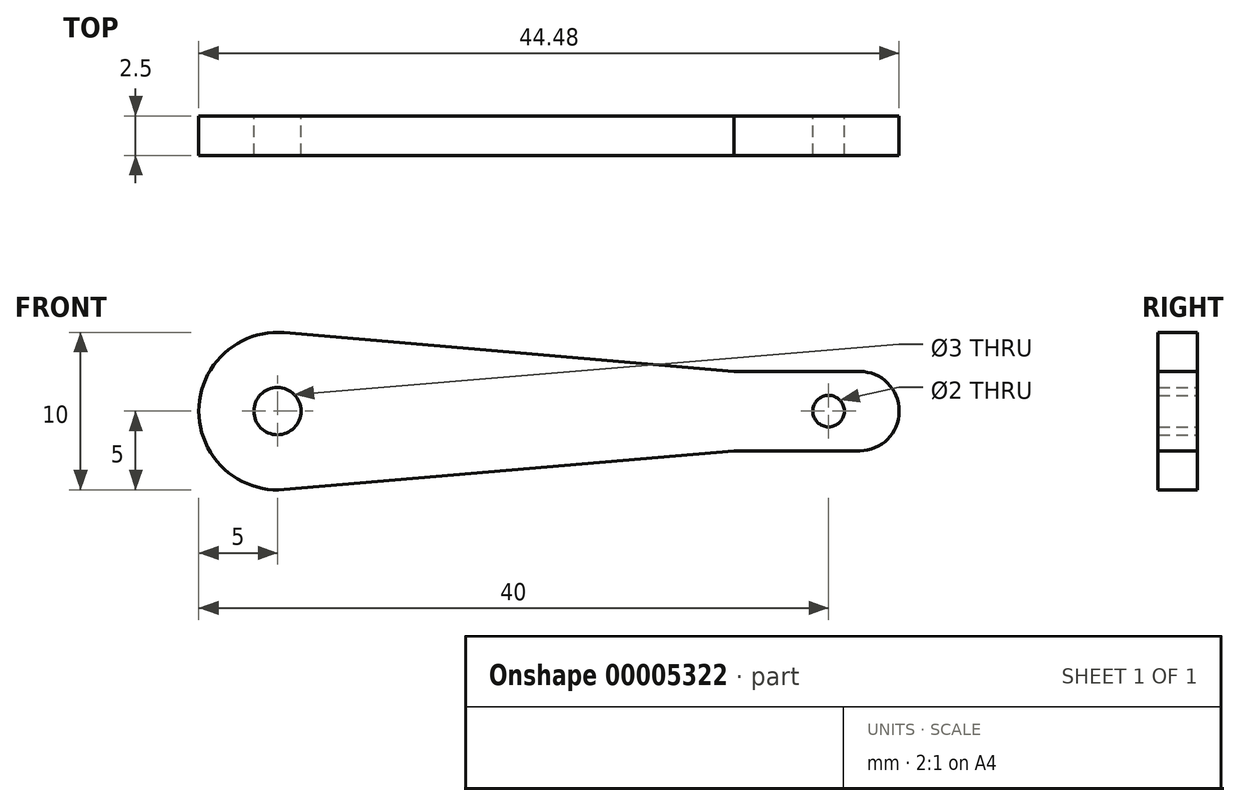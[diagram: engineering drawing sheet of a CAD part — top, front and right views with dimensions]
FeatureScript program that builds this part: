
annotation { "Feature Type Name" : "Feature", "Feature Type Description" : "" }
export const myFeature = defineFeature(function(context is Context, id is Id, definition is map)
    precondition{}
    {
        {
            var Q0;
            Q0=qCreatedBy(makeId("Front.planeOp"),FACE);
            var sketch = newSketch(context, id + "F0", { "sketchPlane" : qUnion([Q0])});
            skCircle(sketch, "E0", {"center": v(0, 0) * mm, "radius": 1.5 * mm});
            skArc(sketch, "E1", {"start": v(0.43, 4.98) * mm, "mid": v(-5, 0) * mm, "end": v(0.43, -4.98) * mm});
            skCircle(sketch, "E2", {"center": v(35, 0) * mm, "radius": 1 * mm});
            skLineSegment(sketch, "E3.rect.bottom", {"start": v(36.98, 2.52) * mm, "end": v(28.98, 2.52) * mm});
            skLineSegment(sketch, "E3.rect.top", {"start": v(36.98, -2.52) * mm, "end": v(28.98, -2.52) * mm});
            skLineSegment(sketch, "E3.rect.left", {"start": v(39.48, 0.02) * mm, "end": v(39.48, -0.02) * mm});
            skPoint(sketch, "E3.rect.middle", {"position": v(34.23, 0) * mm});
            skLineSegment(sketch, "E4", {"start": v(28.98, 2.52) * mm, "end": v(0.43, 4.98) * mm});
            skLineSegment(sketch, "E5", {"start": v(28.98, -2.52) * mm, "end": v(0.43, -4.98) * mm});
            skPoint(sketch, "E6.visualSharp", {"position": v(39.48, 2.52) * mm});
            skArc(sketch, "E6.filletArc", {"start": v(39.48, 0.02) * mm, "mid": v(38.75, 1.79) * mm, "end": v(36.98, 2.52) * mm});
            skPoint(sketch, "E7.visualSharp", {"position": v(39.48, -2.52) * mm});
            skArc(sketch, "E7.filletArc", {"start": v(36.98, -2.52) * mm, "mid": v(38.75, -1.79) * mm, "end": v(39.48, -0.02) * mm});
            skSolve(sketch);
        }
        {
            var Q0;
            Q0=makeQuery(id+"F0.imprint","IMPRINT",FACE,{"disambiguationData":[TD([[makeQuery(id+"F0.imprint","IMPRINT",EDGE,{"derivedFrom":sQuery(id+"F0.wireOp",EDGE,"E0")}),-1.0]])]});
            extrude(context, id + "F1", {"entities" : qUnion([Q0]), "depth" : 2.5 * mm});
        }
    });
